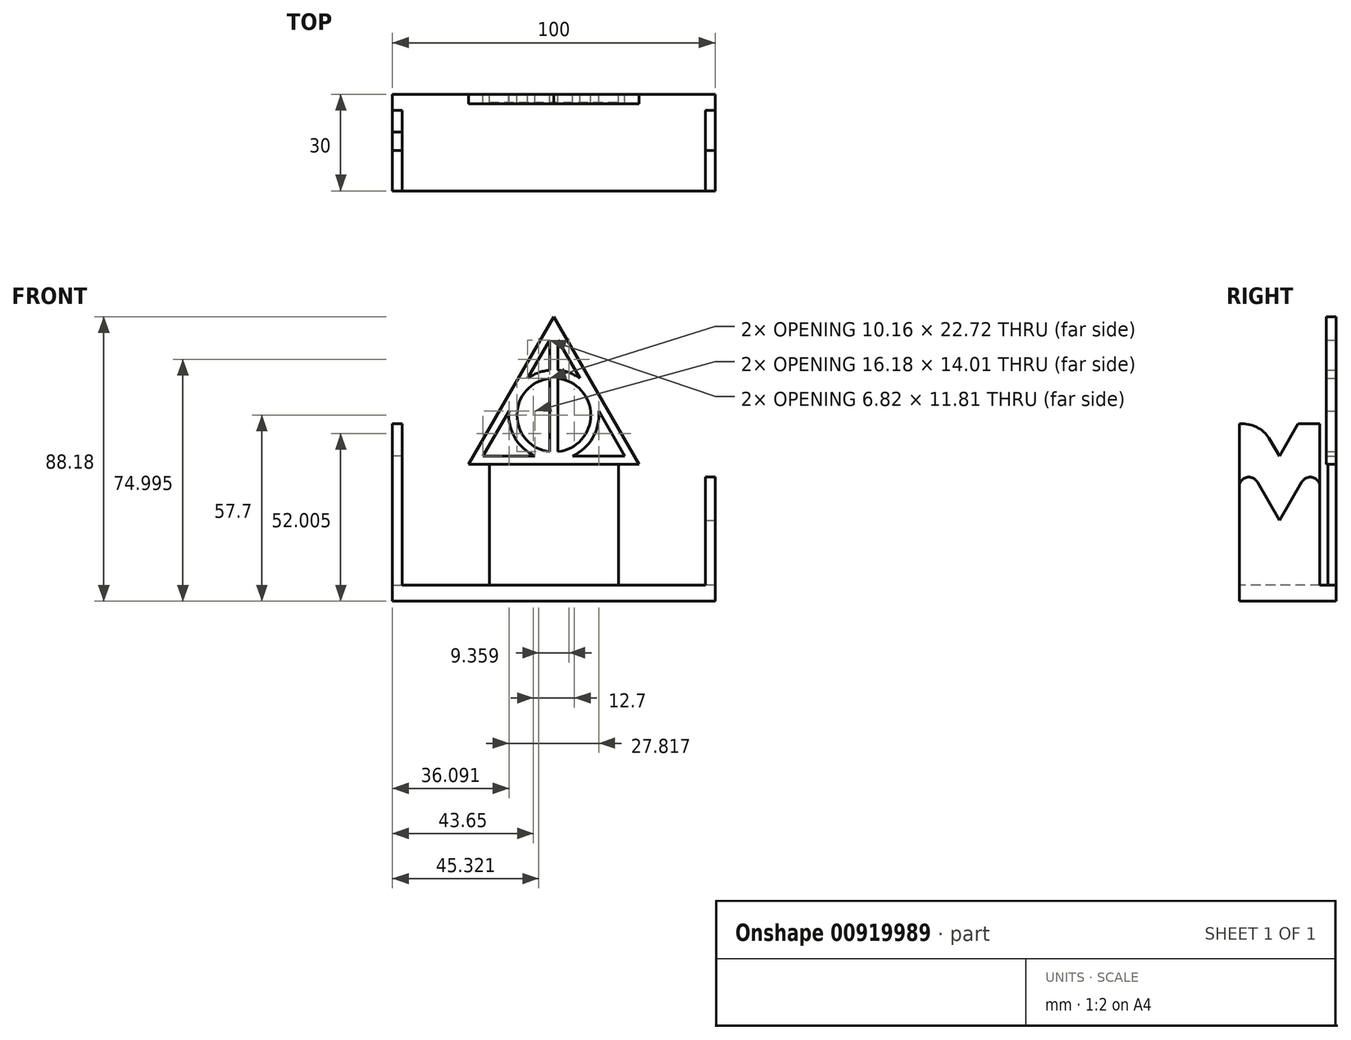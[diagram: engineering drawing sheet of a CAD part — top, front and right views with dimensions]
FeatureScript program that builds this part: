
annotation { "Feature Type Name" : "Feature", "Feature Type Description" : "" }
export const myFeature = defineFeature(function(context is Context, id is Id, definition is map)
    precondition{}
    {
        {
            var Q0;
            Q0=qCreatedBy(makeId("Front.planeOp"),FACE);
            var sketch = newSketch(context, id + "F0", { "sketchPlane" : qUnion([Q0])});
            skLineSegment(sketch, "E0", {"start": v(-22, 0) * mm, "end": v(-5.82, 0) * mm});
            skLineSegment(sketch, "E1", {"start": v(22, 0) * mm, "end": v(13.9, 14) * mm});
            skLineSegment(sketch, "E2", {"start": v(-1.27, 35.9) * mm, "end": v(-8.09, 24.1) * mm});
            skLineSegment(sketch, "E3.0", {"start": v(26.4, -2.54) * mm, "end": v(0, 43.18) * mm});
            skLineSegment(sketch, "E4.0", {"start": v(0, 43.18) * mm, "end": v(-26.4, -2.54) * mm});
            skLineSegment(sketch, "E5.0", {"start": v(-26.4, -2.54) * mm, "end": v(26.4, -2.54) * mm});
            skArc(sketch, "E6.0", {"start": v(-1.27, 26.61) * mm, "mid": v(-4.85, 25.8) * mm, "end": v(-8.09, 24.1) * mm});
            skArc(sketch, "E7.0", {"start": v(-1.27, 24.06) * mm, "mid": v(-11.43, 12.7) * mm, "end": v(-1.27, 1.34) * mm});
            skLineSegment(sketch, "E8.0", {"start": v(-1.27, 35.9) * mm, "end": v(-1.27, 26.61) * mm});
            skLineSegment(sketch, "E9.0", {"start": v(1.27, 35.9) * mm, "end": v(1.27, 26.61) * mm});
            skLineSegment(sketch, "E10.trimOffspring", {"start": v(1.27, 24.06) * mm, "end": v(1.27, 1.34) * mm});
            skLineSegment(sketch, "E11.trimOffspring", {"start": v(-1.27, 24.06) * mm, "end": v(-1.27, 1.34) * mm});
            skArc(sketch, "E12.trimOffspring", {"start": v(-13.9, 14) * mm, "mid": v(-12.1, 5.72) * mm, "end": v(-5.82, 0) * mm});
            skLineSegment(sketch, "E13.trimOffspring", {"start": v(-13.9, 14) * mm, "end": v(-22, 0) * mm});
            skLineSegment(sketch, "E14.trimOffspring", {"start": v(8.09, 24.1) * mm, "end": v(1.27, 35.9) * mm});
            skArc(sketch, "E15.trimOffspring", {"start": v(8.09, 24.1) * mm, "mid": v(4.85, 25.8) * mm, "end": v(1.27, 26.61) * mm});
            skArc(sketch, "E16.trimOffspring", {"start": v(5.82, 0) * mm, "mid": v(12.1, 5.72) * mm, "end": v(13.9, 14) * mm});
            skLineSegment(sketch, "E17.trimOffspring", {"start": v(5.82, 0) * mm, "end": v(22, 0) * mm});
            skArc(sketch, "E18.trimOffspring", {"start": v(1.27, 1.34) * mm, "mid": v(11.43, 12.7) * mm, "end": v(1.27, 24.06) * mm});
            skLineSegment(sketch, "E19.filletArc", {"start": v(-26.4, -2.54) * mm, "end": v(-26.4, -2.54) * mm});
            skLineSegment(sketch, "E20.filletArc", {"start": v(26.4, -2.54) * mm, "end": v(26.4, -2.54) * mm});
            skSolve(sketch);
        }
        {
            var Q0;
            Q0 = qSketchRegion(id + "F0", true);
            extrude(context, id + "F1", {"entities" : qUnion([Q0]), "depth" : 3 * mm, "offsetDistance" : 25.4 * mm});
        }
        {
            var Q0;
            Q0=qCreatedBy(makeId("Front.planeOp"),FACE);
            var sketch = newSketch(context, id + "F2", { "sketchPlane" : qUnion([Q0])});
            skLineSegment(sketch, "E21", {"start": v(-20, 0) * mm, "end": v(-20, -40) * mm});
            skLineSegment(sketch, "E22", {"start": v(-20, -40) * mm, "end": v(20, -40) * mm});
            skLineSegment(sketch, "E23", {"start": v(20, -40) * mm, "end": v(20, 0) * mm});
            skLineSegment(sketch, "E24", {"start": v(20, 0) * mm, "end": v(-20, 0) * mm});
            skLineSegment(sketch, "E25", {"start": v(0, -40) * mm, "end": v(0, 0) * mm});
            skSolve(sketch);
        }
        {
            var Q0;
            Q0 = qSketchRegion(id + "F2", true);
            extrude(context, id + "F3", {"entities" : qUnion([Q0]), "operationType" : NewBodyOperationType.ADD, "depth" : 2.5 * mm, "offsetDistance" : 25 * mm});
        }
        {
            var Q0;
            Q0=qCreatedBy(makeId("Front.planeOp"),FACE);
            var sketch = newSketch(context, id + "F4", { "sketchPlane" : qUnion([Q0])});
            skLineSegment(sketch, "E26.0", {"start": v(-20, -40) * mm, "end": v(20, -40) * mm});
            skLineSegment(sketch, "E27", {"start": v(-20, -40) * mm, "end": v(-50, -40) * mm});
            skLineSegment(sketch, "E28", {"start": v(-50, -40) * mm, "end": v(-50, -45) * mm});
            skLineSegment(sketch, "E29", {"start": v(-50, -45) * mm, "end": v(50, -45) * mm});
            skLineSegment(sketch, "E30", {"start": v(50, -45) * mm, "end": v(50, -40) * mm});
            skLineSegment(sketch, "E31", {"start": v(50, -40) * mm, "end": v(20, -40) * mm});
            skSolve(sketch);
        }
        {
            var Q0;
            Q0 = qSketchRegion(id + "F4", true);
            extrude(context, id + "F5", {"entities" : qUnion([Q0]), "operationType" : NewBodyOperationType.ADD, "depth" : 30 * mm, "offsetDistance" : 25 * mm});
        }
        {
            var Q0;
            Q0=makeQuery(id+"F5.opExtrude","SWEPT_FACE",FACE,{"disambiguationData":[OSD([sQuery(id+"F4.wireOp",EDGE,"E26.0"),sQuery(id+"F4.wireOp",EDGE,"E27"),sQuery(id+"F4.wireOp",EDGE,"E31")])]});
            var sketch = newSketch(context, id + "F6", { "sketchPlane" : qUnion([Q0])});
            skLineSegment(sketch, "E32.bottom", {"start": v(-50, -5) * mm, "end": v(-47, -5) * mm});
            skLineSegment(sketch, "E32.top", {"start": v(-50, -30) * mm, "end": v(-47, -30) * mm});
            skLineSegment(sketch, "E32.left", {"start": v(-50, -5) * mm, "end": v(-50, -30) * mm});
            skLineSegment(sketch, "E32.right", {"start": v(-47, -5) * mm, "end": v(-47, -30) * mm});
            skLineSegment(sketch, "E33.bottom", {"start": v(50, -5) * mm, "end": v(47, -5) * mm});
            skLineSegment(sketch, "E33.top", {"start": v(50, -30) * mm, "end": v(47, -30) * mm});
            skLineSegment(sketch, "E33.left", {"start": v(50, -5) * mm, "end": v(50, -30) * mm});
            skLineSegment(sketch, "E33.right", {"start": v(47, -5) * mm, "end": v(47, -30) * mm});
            skSolve(sketch);
        }
        {
            var Q0;
            Q0 = qSketchRegion(id + "F6", true);
            extrude(context, id + "F7", {"entities" : qUnion([Q0]), "operationType" : NewBodyOperationType.ADD, "depth" : 50 * mm, "offsetDistance" : 25 * mm});
        }
        {
            var Q0;
            Q0=makeQuery(id+"F7.boolean.opBoolean","MERGE",FACE,{"derivedFrom":[makeQuery(id+"F5.opExtrude","SWEPT_FACE",FACE,{"disambiguationData":[OSD([sQuery(id+"F4.wireOp",EDGE,"E28")])]}),makeQuery(id+"F7.opExtrude","SWEPT_FACE",FACE,{"disambiguationData":[OSD([sQuery(id+"F6.wireOp",EDGE,"E32.left")])]})]});
            var sketch = newSketch(context, id + "F8", { "sketchPlane" : qUnion([Q0])});
            skLineSegment(sketch, "E34", {"start": v(11.73, 10) * mm, "end": v(17.5, 0) * mm});
            skPoint(sketch, "E34.endSnap0", {"position": v(17.5, 10) * mm});
            skLineSegment(sketch, "E35", {"start": v(17.5, 0) * mm, "end": v(23.27, 10) * mm});
            skLineSegment(sketch, "E36", {"start": v(23.27, 10) * mm, "end": v(11.73, 10) * mm});
            skLineSegment(sketch, "E37", {"start": v(17.5, 0) * mm, "end": v(17.5, 10) * mm, "construction": true});
            skSolve(sketch);
        }
        {
            var Q0;
            Q0 = qSketchRegion(id + "F8", true);
            extrude(context, id + "F9", {"entities" : qUnion([Q0]), "operationType" : NewBodyOperationType.REMOVE, "oppositeDirection" : true, "depth" : 25 * mm, "offsetDistance" : 25 * mm});
        }
        {
            var Q0;
            Q0=makeQuery(id+"F7.boolean.opBoolean","MERGE",FACE,{"derivedFrom":[makeQuery(id+"F5.opExtrude","SWEPT_FACE",FACE,{"disambiguationData":[OSD([sQuery(id+"F4.wireOp",EDGE,"E30")])]}),makeQuery(id+"F7.opExtrude","SWEPT_FACE",FACE,{"disambiguationData":[OSD([sQuery(id+"F6.wireOp",EDGE,"E33.left")])]})]});
            var sketch = newSketch(context, id + "F10", { "sketchPlane" : qUnion([Q0])});
            skLineSegment(sketch, "E38", {"start": v(-34.82, 10) * mm, "end": v(-17.5, -20) * mm});
            skPoint(sketch, "E38.endSnap0", {"position": v(-17.5, 10) * mm});
            skLineSegment(sketch, "E39", {"start": v(-17.5, -20) * mm, "end": v(-0.18, 10) * mm});
            skLineSegment(sketch, "E40", {"start": v(-0.18, 10) * mm, "end": v(-34.82, 10) * mm});
            skLineSegment(sketch, "E41", {"start": v(-17.5, 10) * mm, "end": v(-17.5, -20) * mm});
            skSolve(sketch);
        }
        {
            var Q0;
            Q0 = qSketchRegion(id + "F10", true);
            extrude(context, id + "F11", {"entities" : qUnion([Q0]), "operationType" : NewBodyOperationType.REMOVE, "oppositeDirection" : true, "depth" : 10 * mm, "offsetDistance" : 25 * mm});
        }
        {
            var Q0;
            Q0=makeQuery(id+"F9.boolean.opBoolean","COPY",EDGE,{"derivedFrom":makeQuery(id+"F9.opExtrude","SWEPT_EDGE",EDGE,{"disambiguationData":[OSD([sQuery(id+"F6.wireOp",EDGE,"E32.left"),sQuery(id+"F8.wireOp",EDGE,"E34"),sQuery(id+"F8.wireOp",EDGE,"E36")])]})});
            var Q1;
            Q1=makeQuery(id+"F9.boolean.opBoolean","COPY",EDGE,{"derivedFrom":makeQuery(id+"F9.opExtrude","SWEPT_EDGE",EDGE,{"disambiguationData":[OSD([sQuery(id+"F6.wireOp",EDGE,"E32.left"),sQuery(id+"F8.wireOp",EDGE,"E35"),sQuery(id+"F8.wireOp",EDGE,"E36")])]})});
            fillet(context, id + "F12", {"entities" : qUnion([Q0, Q1]), "radius" : 10 * mm, "tangentPropagation" : true, "allowEdgeOverflow" : false});
        }
        {
            var Q0;
            Q0=makeQuery(id+"F11.boolean.opBoolean","INTERSECT",EDGE,{"derivedFrom":[makeQuery(id+"F7.boolean.opBoolean","MERGE",FACE,{"derivedFrom":[makeQuery(id+"F5.opExtrude","CAP_FACE",FACE,{"disambiguationData":[OSD([sQuery(id+"F4.wireOp",EDGE,"E26.0"),sQuery(id+"F4.wireOp",EDGE,"E27"),sQuery(id+"F4.wireOp",EDGE,"E28"),sQuery(id+"F4.wireOp",EDGE,"E29"),sQuery(id+"F4.wireOp",EDGE,"E30"),sQuery(id+"F4.wireOp",EDGE,"E31")])],"isStart":false}),makeQuery(id+"F7.opExtrude","SWEPT_FACE",FACE,{"disambiguationData":[OSD([sQuery(id+"F6.wireOp",EDGE,"E32.top")])]}),makeQuery(id+"F7.opExtrude","SWEPT_FACE",FACE,{"disambiguationData":[OSD([sQuery(id+"F6.wireOp",EDGE,"E33.top")])]})]}),makeQuery(id+"F11.opExtrude","SWEPT_FACE",FACE,{"disambiguationData":[OSD([sQuery(id+"F10.wireOp",EDGE,"E38")])]})]});
            var Q1;
            Q1=makeQuery(id+"F11.boolean.opBoolean","INTERSECT",EDGE,{"derivedFrom":[makeQuery(id+"F7.opExtrude","SWEPT_FACE",FACE,{"disambiguationData":[OSD([sQuery(id+"F6.wireOp",EDGE,"E33.bottom")])]}),makeQuery(id+"F11.opExtrude","SWEPT_FACE",FACE,{"disambiguationData":[OSD([sQuery(id+"F10.wireOp",EDGE,"E39")])]})]});
            fillet(context, id + "F13", {"entities" : qUnion([Q0, Q1]), "radius" : 3 * mm, "tangentPropagation" : true, "allowEdgeOverflow" : false});
        }
    });
